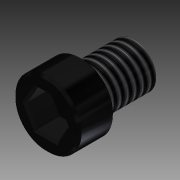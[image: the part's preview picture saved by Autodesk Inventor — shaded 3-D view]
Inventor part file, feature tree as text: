
AUTODESK INVENTOR PART (.ipt)
format: ipt  version: 2013 (Build 170138000, 138)  size: 117,760 bytes
history: native  units: in
note: dims shown in document units (in); Inventor stores cm internally (conversion verified against a paired STEP export)
features: extrude x3, sketch x1, thread x1, chamfer x1
ambient origin geometry x8: Origin, YZ Plane, XZ Plane, XY Plane, X Axis, Y Axis, Z Axis, Center Point
bodies: Solid1 (feature_tree)
feature tree (6):
  sketch  "Sketch1"  dims[d0=0.275in d1=0.185in d2=0.15in d3=0.15in d4=0.0in d5=0.215in d6=0.0in d7=0.05in d8=0.0in d9=1.0in d10=0.0in d11=0.01in d12=0.125in d13=45.0deg]
  extrude  "Extrusion1"  Depth=0.185in
  extrude  "Extrusion2"  Depth=0.15in
  extrude  "Extrusion3"  Depth=0.15in TaperAngle=0.0deg
  thread  "Thread1"  [1 undecoded]
  chamfer  "Chamfer1"  Distance=0.05in
note: 1 required parameter value undecoded (feature->parameter linkage not recoverable at this tier; creation-order binding heuristic only, values carry confidence <= 0.55)
